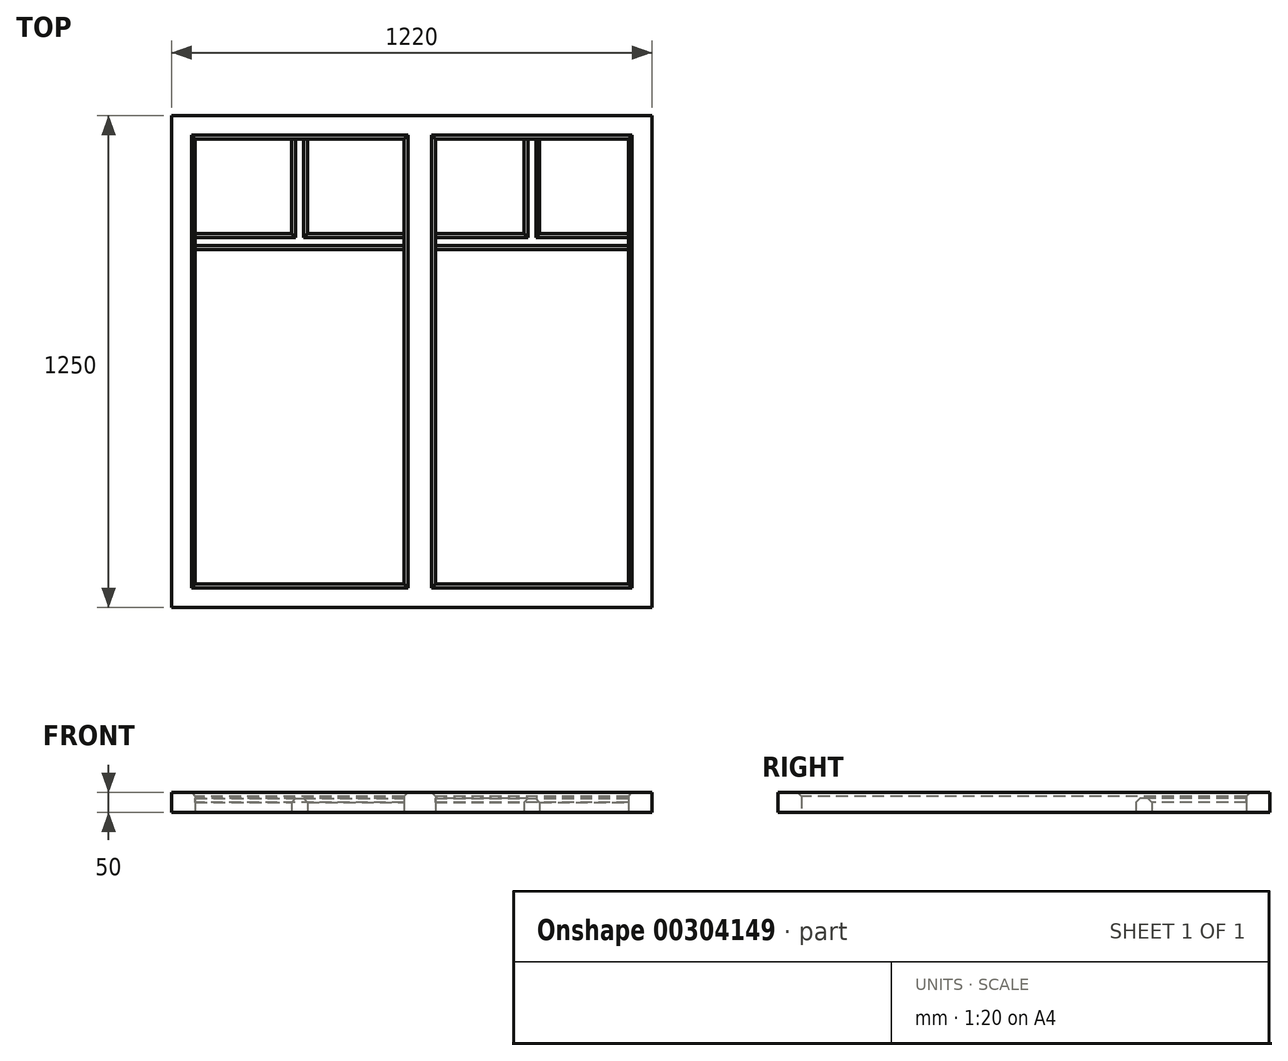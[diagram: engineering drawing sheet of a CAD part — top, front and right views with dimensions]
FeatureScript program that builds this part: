
annotation { "Feature Type Name" : "Feature", "Feature Type Description" : "" }
export const myFeature = defineFeature(function(context is Context, id is Id, definition is map)
    precondition{}
    {
        {
            var Q0;
            Q0=qCreatedBy(makeId("Top.planeOp"),FACE);
            var sketch = newSketch(context, id + "F0", { "sketchPlane" : qUnion([Q0])});
            skLineSegment(sketch, "E0.bottom", {"start": v(-409.69, 695.2) * mm, "end": v(810.31, 695.2) * mm});
            skLineSegment(sketch, "E0.top", {"start": v(-409.69, -554.8) * mm, "end": v(810.31, -554.8) * mm});
            skLineSegment(sketch, "E0.left", {"start": v(-409.69, 695.2) * mm, "end": v(-409.69, -554.8) * mm});
            skLineSegment(sketch, "E0.right", {"start": v(810.31, 695.2) * mm, "end": v(810.31, -554.8) * mm});
            skLineSegment(sketch, "E1.bottom", {"start": v(-349.69, 355.2) * mm, "end": v(180.31, 355.2) * mm});
            skLineSegment(sketch, "E1.top", {"start": v(-349.69, -494.8) * mm, "end": v(180.31, -494.8) * mm});
            skLineSegment(sketch, "E1.left", {"start": v(-349.69, 355.2) * mm, "end": v(-349.69, -494.8) * mm});
            skLineSegment(sketch, "E1.right", {"start": v(180.31, 355.2) * mm, "end": v(180.31, -494.8) * mm});
            skLineSegment(sketch, "E2.bottom", {"start": v(260.31, 355.2) * mm, "end": v(750.31, 355.2) * mm});
            skLineSegment(sketch, "E2.top", {"start": v(260.31, -494.8) * mm, "end": v(750.31, -494.8) * mm});
            skLineSegment(sketch, "E2.left", {"start": v(260.31, 355.2) * mm, "end": v(260.31, -494.8) * mm});
            skLineSegment(sketch, "E2.right", {"start": v(750.31, 355.2) * mm, "end": v(750.31, -494.8) * mm});
            skLineSegment(sketch, "E3.bottom", {"start": v(-349.69, 635.2) * mm, "end": v(-104.69, 635.2) * mm});
            skLineSegment(sketch, "E3.top", {"start": v(-349.69, 395.2) * mm, "end": v(-104.69, 395.2) * mm});
            skLineSegment(sketch, "E3.left", {"start": v(-349.69, 635.2) * mm, "end": v(-349.69, 395.2) * mm});
            skLineSegment(sketch, "E3.right", {"start": v(-104.69, 635.2) * mm, "end": v(-104.69, 395.2) * mm});
            skLineSegment(sketch, "E4.bottom", {"start": v(-64.69, 635.2) * mm, "end": v(180.31, 635.2) * mm});
            skLineSegment(sketch, "E4.top", {"start": v(-64.69, 395.2) * mm, "end": v(180.31, 395.2) * mm});
            skLineSegment(sketch, "E4.left", {"start": v(-64.69, 635.2) * mm, "end": v(-64.69, 395.2) * mm});
            skLineSegment(sketch, "E4.right", {"start": v(180.31, 635.2) * mm, "end": v(180.31, 395.2) * mm});
            skLineSegment(sketch, "E5.bottom", {"start": v(260.31, 635.2) * mm, "end": v(485.31, 635.2) * mm});
            skLineSegment(sketch, "E5.top", {"start": v(260.31, 395.2) * mm, "end": v(485.31, 395.2) * mm});
            skLineSegment(sketch, "E5.left", {"start": v(260.31, 635.2) * mm, "end": v(260.31, 395.2) * mm});
            skLineSegment(sketch, "E5.right", {"start": v(485.31, 635.2) * mm, "end": v(485.31, 395.2) * mm});
            skLineSegment(sketch, "E6.bottom", {"start": v(525.31, 635.2) * mm, "end": v(750.31, 635.2) * mm});
            skLineSegment(sketch, "E6.top", {"start": v(525.31, 395.2) * mm, "end": v(750.31, 395.2) * mm});
            skLineSegment(sketch, "E6.left", {"start": v(525.31, 635.2) * mm, "end": v(525.31, 395.2) * mm});
            skLineSegment(sketch, "E6.right", {"start": v(750.31, 635.2) * mm, "end": v(750.31, 395.2) * mm});
            skLineSegment(sketch, "E7", {"start": v(-349.69, 395.2) * mm, "end": v(-349.69, 355.2) * mm});
            skLineSegment(sketch, "E8", {"start": v(-104.69, 635.2) * mm, "end": v(-64.69, 635.2) * mm});
            skLineSegment(sketch, "E9", {"start": v(180.31, 395.2) * mm, "end": v(180.31, 355.2) * mm});
            skLineSegment(sketch, "E10", {"start": v(260.31, 395.2) * mm, "end": v(260.31, 355.2) * mm});
            skLineSegment(sketch, "E11", {"start": v(485.31, 635.2) * mm, "end": v(525.31, 635.2) * mm});
            skLineSegment(sketch, "E12", {"start": v(750.31, 395.2) * mm, "end": v(750.31, 355.2) * mm});
            skSolve(sketch);
        }
        {
            var Q0;
            Q0=makeQuery(id+"F0.imprint","IMPRINT",FACE,{"disambiguationData":[TD([[makeQuery(id+"F0.imprint","IMPRINT",EDGE,{"derivedFrom":sQuery(id+"F0.wireOp",EDGE,"E0.bottom")}),-1.0]])]});
            extrude(context, id + "F1", {"entities" : qUnion([Q0]), "depth" : 50 * mm});
        }
        {
            var Q0;
            Q0=makeQuery(id+"F0.imprint","IMPRINT",FACE,{"disambiguationData":[TD([[makeQuery(id+"F0.imprint","IMPRINT",EDGE,{"derivedFrom":sQuery(id+"F0.wireOp",EDGE,"E1.bottom")}),1.0]])]});
            var Q1;
            Q1=makeQuery(id+"F0.imprint","IMPRINT",FACE,{"disambiguationData":[TD([[makeQuery(id+"F0.imprint","IMPRINT",EDGE,{"derivedFrom":sQuery(id+"F0.wireOp",EDGE,"E2.bottom")}),1.0]])]});
            extrude(context, id + "F2", {"entities" : qUnion([Q0, Q1]), "depth" : 35 * mm, "offsetDistance" : 25 * mm});
        }
        {
            var Q0;
            Q0=makeQuery(id+"F1.opExtrude","CAP_EDGE",EDGE,{"disambiguationData":[OSD([sQuery(id+"F0.wireOp",EDGE,"E3.left")])],"isStart":false});
            var Q1;
            Q1=makeQuery(id+"F1.opExtrude","CAP_EDGE",EDGE,{"disambiguationData":[OSD([sQuery(id+"F0.wireOp",EDGE,"E3.bottom")])],"isStart":false});
            var Q2;
            Q2=makeQuery(id+"F1.opExtrude","CAP_EDGE",EDGE,{"disambiguationData":[OSD([sQuery(id+"F0.wireOp",EDGE,"E3.right")])],"isStart":false});
            var Q3;
            Q3=makeQuery(id+"F1.opExtrude","CAP_EDGE",EDGE,{"disambiguationData":[OSD([sQuery(id+"F0.wireOp",EDGE,"E3.top")])],"isStart":false});
            var Q4;
            Q4=makeQuery(id+"F1.opExtrude","CAP_EDGE",EDGE,{"disambiguationData":[OSD([sQuery(id+"F0.wireOp",EDGE,"E4.top")])],"isStart":false});
            var Q5;
            Q5=makeQuery(id+"F1.opExtrude","CAP_EDGE",EDGE,{"disambiguationData":[OSD([sQuery(id+"F0.wireOp",EDGE,"E4.bottom")])],"isStart":false});
            var Q6;
            Q6=makeQuery(id+"F1.opExtrude","CAP_EDGE",EDGE,{"disambiguationData":[OSD([sQuery(id+"F0.wireOp",EDGE,"E4.left")])],"isStart":false});
            var Q7;
            Q7=makeQuery(id+"F1.opExtrude","CAP_EDGE",EDGE,{"disambiguationData":[OSD([sQuery(id+"F0.wireOp",EDGE,"E4.right")])],"isStart":false});
            var Q8;
            Q8=makeQuery(id+"F1.opExtrude","CAP_EDGE",EDGE,{"disambiguationData":[OSD([sQuery(id+"F0.wireOp",EDGE,"E5.left")])],"isStart":false});
            var Q9;
            Q9=makeQuery(id+"F1.opExtrude","CAP_EDGE",EDGE,{"disambiguationData":[OSD([sQuery(id+"F0.wireOp",EDGE,"E5.bottom")])],"isStart":false});
            var Q10;
            Q10=makeQuery(id+"F1.opExtrude","CAP_EDGE",EDGE,{"disambiguationData":[OSD([sQuery(id+"F0.wireOp",EDGE,"E5.right")])],"isStart":false});
            var Q11;
            Q11=makeQuery(id+"F1.opExtrude","CAP_EDGE",EDGE,{"disambiguationData":[OSD([sQuery(id+"F0.wireOp",EDGE,"E5.top")])],"isStart":false});
            var Q12;
            Q12=makeQuery(id+"F1.opExtrude","CAP_EDGE",EDGE,{"disambiguationData":[OSD([sQuery(id+"F0.wireOp",EDGE,"E6.bottom")])],"isStart":false});
            var Q13;
            Q13=makeQuery(id+"F1.opExtrude","CAP_EDGE",EDGE,{"disambiguationData":[OSD([sQuery(id+"F0.wireOp",EDGE,"E6.left")])],"isStart":false});
            var Q14;
            Q14=makeQuery(id+"F1.opExtrude","CAP_EDGE",EDGE,{"disambiguationData":[OSD([sQuery(id+"F0.wireOp",EDGE,"E6.top")])],"isStart":false});
            var Q15;
            Q15=makeQuery(id+"F1.opExtrude","CAP_EDGE",EDGE,{"disambiguationData":[OSD([sQuery(id+"F0.wireOp",EDGE,"E6.right")])],"isStart":false});
            var Q16;
            Q16=makeQuery(id+"F1.opExtrude","CAP_EDGE",EDGE,{"disambiguationData":[OSD([sQuery(id+"F0.wireOp",EDGE,"E2.bottom")])],"isStart":false});
            var Q17;
            Q17=makeQuery(id+"F1.opExtrude","CAP_EDGE",EDGE,{"disambiguationData":[OSD([sQuery(id+"F0.wireOp",EDGE,"E2.right")])],"isStart":false});
            var Q18;
            Q18=makeQuery(id+"F1.opExtrude","CAP_EDGE",EDGE,{"disambiguationData":[OSD([sQuery(id+"F0.wireOp",EDGE,"E2.top")])],"isStart":false});
            var Q19;
            Q19=makeQuery(id+"F1.opExtrude","CAP_EDGE",EDGE,{"disambiguationData":[OSD([sQuery(id+"F0.wireOp",EDGE,"E2.left")])],"isStart":false});
            var Q20;
            Q20=makeQuery(id+"F1.opExtrude","CAP_EDGE",EDGE,{"disambiguationData":[OSD([sQuery(id+"F0.wireOp",EDGE,"E1.right")])],"isStart":false});
            var Q21;
            Q21=makeQuery(id+"F1.opExtrude","CAP_EDGE",EDGE,{"disambiguationData":[OSD([sQuery(id+"F0.wireOp",EDGE,"E1.bottom")])],"isStart":false});
            var Q22;
            Q22=makeQuery(id+"F1.opExtrude","CAP_EDGE",EDGE,{"disambiguationData":[OSD([sQuery(id+"F0.wireOp",EDGE,"E1.left")])],"isStart":false});
            var Q23;
            Q23=makeQuery(id+"F1.opExtrude","CAP_EDGE",EDGE,{"disambiguationData":[OSD([sQuery(id+"F0.wireOp",EDGE,"E1.top")])],"isStart":false});
            var Q24;
            Q24=makeQuery(id+"F2.opExtrude","CAP_EDGE",EDGE,{"disambiguationData":[OSD([sQuery(id+"F0.wireOp",EDGE,"E1.bottom")])],"isStart":false});
            var Q25;
            Q25=makeQuery(id+"F2.opExtrude","CAP_EDGE",EDGE,{"disambiguationData":[OSD([sQuery(id+"F0.wireOp",EDGE,"E4.top")])],"isStart":false});
            var Q26;
            Q26=makeQuery(id+"F2.opExtrude","CAP_EDGE",EDGE,{"disambiguationData":[OSD([sQuery(id+"F0.wireOp",EDGE,"E4.left")])],"isStart":false});
            var Q27;
            Q27=makeQuery(id+"F2.opExtrude","CAP_EDGE",EDGE,{"disambiguationData":[OSD([sQuery(id+"F0.wireOp",EDGE,"E3.right")])],"isStart":false});
            var Q28;
            Q28=makeQuery(id+"F2.opExtrude","CAP_EDGE",EDGE,{"disambiguationData":[OSD([sQuery(id+"F0.wireOp",EDGE,"E3.top")])],"isStart":false});
            var Q29;
            Q29=makeQuery(id+"F2.opExtrude","CAP_EDGE",EDGE,{"disambiguationData":[OSD([sQuery(id+"F0.wireOp",EDGE,"E2.bottom")])],"isStart":false});
            var Q30;
            Q30=makeQuery(id+"F2.opExtrude","CAP_EDGE",EDGE,{"disambiguationData":[OSD([sQuery(id+"F0.wireOp",EDGE,"E5.top")])],"isStart":false});
            var Q31;
            Q31=makeQuery(id+"F2.opExtrude","CAP_EDGE",EDGE,{"disambiguationData":[OSD([sQuery(id+"F0.wireOp",EDGE,"E6.left")])],"isStart":false});
            var Q32;
            Q32=makeQuery(id+"F2.opExtrude","CAP_EDGE",EDGE,{"disambiguationData":[OSD([sQuery(id+"F0.wireOp",EDGE,"E6.top")])],"isStart":false});
            var Q33;
            Q33=makeQuery(id+"F2.opExtrude","CAP_EDGE",EDGE,{"disambiguationData":[OSD([sQuery(id+"F0.wireOp",EDGE,"E5.right")])],"isStart":false});
            chamfer(context, id + "F3", {"entities" : qUnion([Q0, Q1, Q2, Q3, Q4, Q5, Q6, Q7, Q8, Q9, Q10, Q11, Q12, Q13, Q14, Q15, Q16, Q17, Q18, Q19, Q20, Q21, Q22, Q23, Q24, Q25, Q26, Q27, Q28, Q29, Q30, Q31, Q32, Q33]), "width" : 10 * mm, "tangentPropagation" : true});
        }
    });
